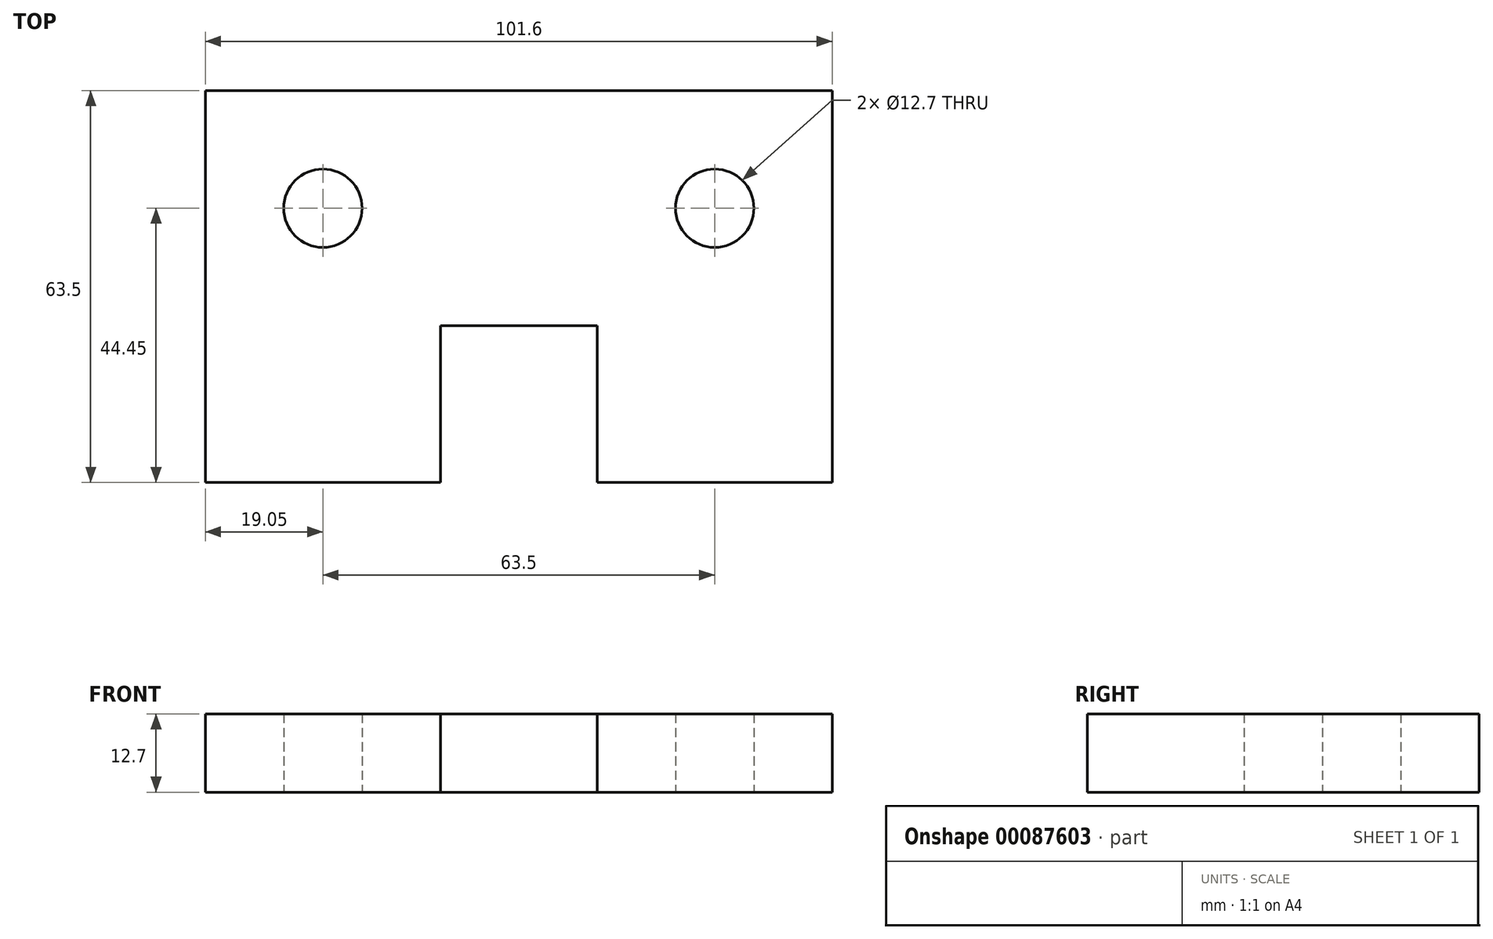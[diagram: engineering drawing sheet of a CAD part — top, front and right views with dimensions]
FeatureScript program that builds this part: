
annotation { "Feature Type Name" : "Feature", "Feature Type Description" : "" }
export const myFeature = defineFeature(function(context is Context, id is Id, definition is map)
    precondition{}
    {
        {
            var Q0;
            Q0=qCreatedBy(makeId("Top.planeOp"),FACE);
            var sketch = newSketch(context, id + "F0", { "sketchPlane" : qUnion([Q0])});
            skLineSegment(sketch, "E0.bottom", {"start": v(0, 0) * mm, "end": v(38.1, 0) * mm});
            skLineSegment(sketch, "E0.top", {"start": v(0, 63.5) * mm, "end": v(101.6, 63.5) * mm});
            skLineSegment(sketch, "E0.left", {"start": v(0, 0) * mm, "end": v(0, 63.5) * mm});
            skLineSegment(sketch, "E0.right", {"start": v(101.6, 0) * mm, "end": v(101.6, 63.5) * mm});
            skLineSegment(sketch, "E1", {"start": v(38.1, 0) * mm, "end": v(38.1, 25.4) * mm});
            skLineSegment(sketch, "E2", {"start": v(38.1, 25.4) * mm, "end": v(63.5, 25.4) * mm});
            skLineSegment(sketch, "E3", {"start": v(63.5, 25.4) * mm, "end": v(63.5, 0) * mm});
            skCircle(sketch, "E4", {"center": v(19.05, 44.45) * mm, "radius": 6.35 * mm});
            skCircle(sketch, "E5", {"center": v(82.55, 44.45) * mm, "radius": 6.35 * mm});
            skLineSegment(sketch, "E6.trimOffspring", {"start": v(63.5, 0) * mm, "end": v(101.6, 0) * mm});
            skLineSegment(sketch, "E7", {"start": v(19.05, 44.45) * mm, "end": v(82.55, 44.45) * mm, "construction": true});
            skSolve(sketch);
        }
        {
            var Q0;
            Q0 = qSketchRegion(id + "F0", true);
            extrude(context, id + "F1", {"entities" : qUnion([Q0]), "depth" : 12.7 * mm});
        }
    });
